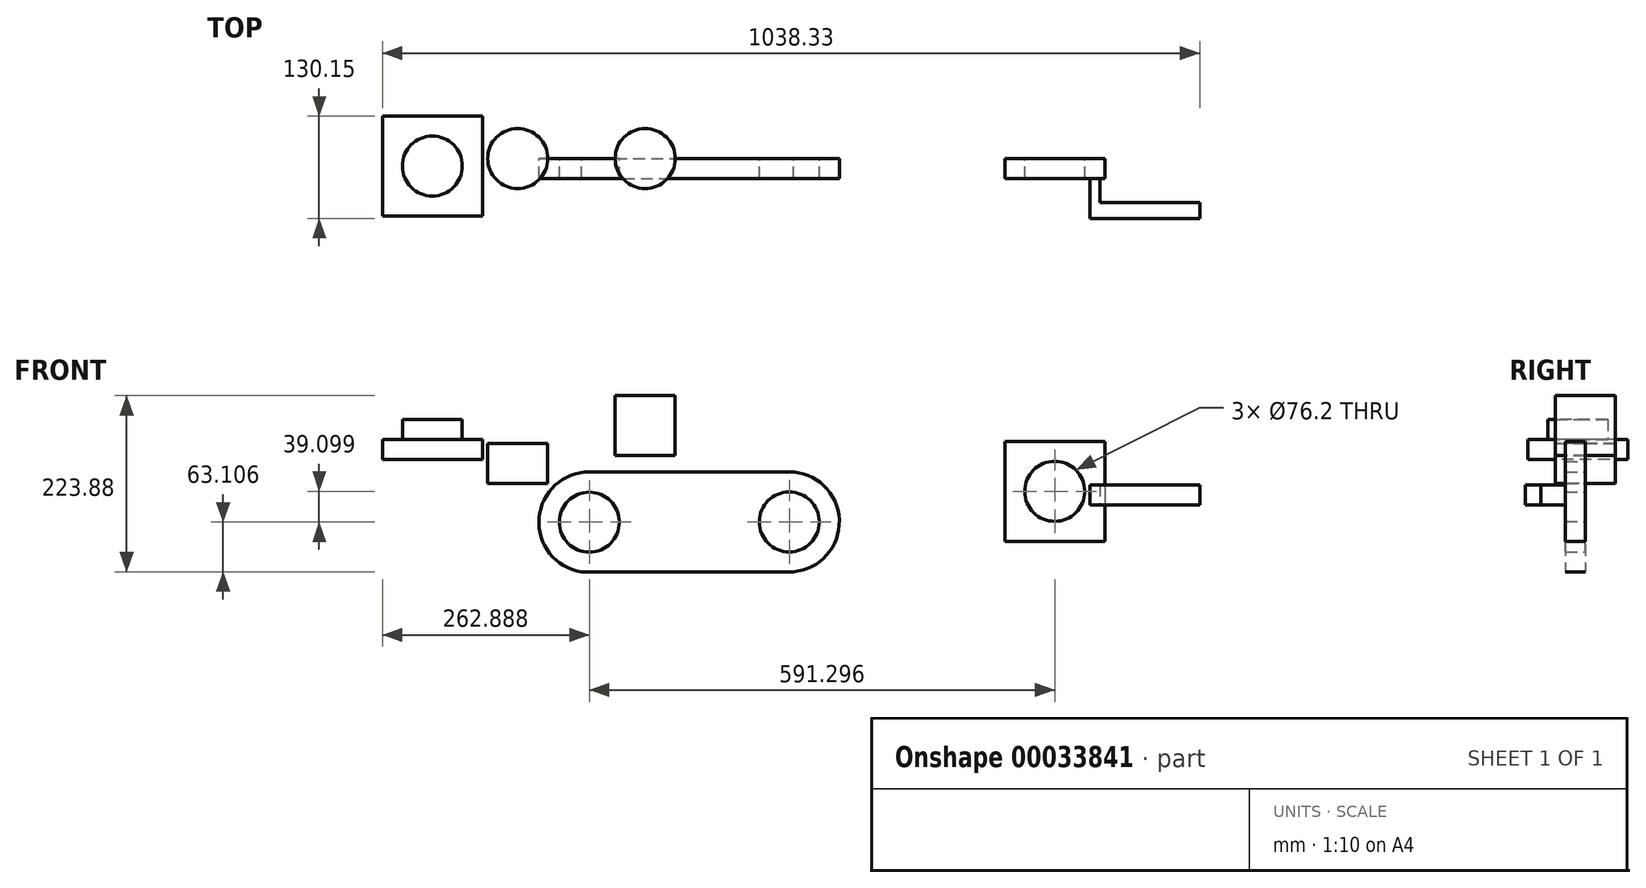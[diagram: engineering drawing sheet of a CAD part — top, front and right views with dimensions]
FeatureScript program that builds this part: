
annotation { "Feature Type Name" : "Feature", "Feature Type Description" : "" }
export const myFeature = defineFeature(function(context is Context, id is Id, definition is map)
    precondition{}
    {
        {
            var Q0;
            Q0=qCreatedBy(makeId("Top.planeOp"),FACE);
            var sketch = newSketch(context, id + "F0", { "sketchPlane" : qUnion([Q0])});
            skLineSegment(sketch, "E0.right", {"start": v(-80.77, 53.95) * mm, "end": v(-80.77, -73.05) * mm});
            skLineSegment(sketch, "E0.left", {"start": v(-207.77, 53.95) * mm, "end": v(-207.77, -73.05) * mm});
            skLineSegment(sketch, "E0.top", {"start": v(-207.77, -73.05) * mm, "end": v(-80.77, -73.05) * mm});
            skLineSegment(sketch, "E0.bottom", {"start": v(-207.77, 53.95) * mm, "end": v(-80.77, 53.95) * mm});
            skSolve(sketch);
        }
        {
            var Q0;
            Q0=makeQuery(id+"F0.imprint","IMPRINT",FACE,{"disambiguationData":[TD([[makeQuery(id+"F0.imprint","IMPRINT",EDGE,{"derivedFrom":sQuery(id+"F0.wireOp",EDGE,"E0.right")}),-1.0]])]});
            extrude(context, id + "F1", {"entities" : qUnion([Q0]), "depth" : 25.4 * mm});
        }
        {
            var Q0;
            Q0=makeQuery(id+"F1.opExtrude","CAP_FACE",FACE,{"disambiguationData":[OSD([sQuery(id+"F0.wireOp",EDGE,"E0.right"),sQuery(id+"F0.wireOp",EDGE,"E0.left"),sQuery(id+"F0.wireOp",EDGE,"E0.top"),sQuery(id+"F0.wireOp",EDGE,"E0.bottom")])],"isStart":false});
            var sketch = newSketch(context, id + "F2", { "sketchPlane" : qUnion([Q0])});
            skCircle(sketch, "E1", {"center": v(-144.27, -9.55) * mm, "radius": 38.1 * mm});
            skPoint(sketch, "E1.centerSnap0", {"position": v(-80.77, -9.55) * mm});
            skPoint(sketch, "E1.centerSnap1", {"position": v(-144.27, 53.95) * mm});
            skSolve(sketch);
        }
        {
            var Q0;
            Q0=makeQuery(id+"F2.imprint","IMPRINT",FACE,{"disambiguationData":[TD([[makeQuery(id+"F2.imprint","IMPRINT",EDGE,{"derivedFrom":sQuery(id+"F2.wireOp",EDGE,"E1")}),1.0]])]});
            extrude(context, id + "F3", {"entities" : qUnion([Q0]), "depth" : 25.4 * mm});
        }
        {
            var Q0;
            Q0=qCreatedBy(makeId("Front.planeOp"),FACE);
            var sketch = newSketch(context, id + "F4", { "sketchPlane" : qUnion([Q0])});
            skCircle(sketch, "E2", {"center": v(309.12, -79.39) * mm, "radius": 38.1 * mm});
            skLineSegment(sketch, "E3", {"start": v(55.12, -15.79) * mm, "end": v(309.12, -15.79) * mm});
            skCircle(sketch, "E4", {"center": v(55.12, -79.68) * mm, "radius": 38.1 * mm});
            skArc(sketch, "E5", {"start": v(314.23, -142.79) * mm, "mid": v(372.67, -76.83) * mm, "end": v(309.12, -15.79) * mm});
            skLineSegment(sketch, "E6", {"start": v(45.07, -142.79) * mm, "end": v(314.23, -142.79) * mm});
            skArc(sketch, "E7", {"start": v(55.12, -15.79) * mm, "mid": v(-8.58, -74.65) * mm, "end": v(45.07, -142.79) * mm});
            skLineSegment(sketch, "E8", {"start": v(55.67, -10.55) * mm, "end": v(55.12, -15.79) * mm});
            skSolve(sketch);
        }
        {
            var Q0;
            Q0=makeQuery(id+"F4.imprint","IMPRINT",FACE,{"disambiguationData":[TD([[makeQuery(id+"F4.imprint","IMPRINT",EDGE,{"derivedFrom":sQuery(id+"F4.wireOp",EDGE,"E2")}),-1.0]])]});
            extrude(context, id + "F5", {"entities" : qUnion([Q0]), "depth" : 25.4 * mm});
        }
        {
            var Q0;
            Q0=qCreatedBy(makeId("Front.planeOp"),FACE);
            var sketch = newSketch(context, id + "F6", { "sketchPlane" : qUnion([Q0])});
            skLineSegment(sketch, "E9", {"start": v(-35.84, 19.93) * mm, "end": v(-35.84, -38.25) * mm, "construction": true});
            skLineSegment(sketch, "E10.bottom", {"start": v(-35.84, 19.93) * mm, "end": v(2.26, 19.93) * mm});
            skLineSegment(sketch, "E10.top", {"start": v(-35.84, -30.87) * mm, "end": v(2.26, -30.87) * mm});
            skLineSegment(sketch, "E10.left", {"start": v(-35.84, 19.93) * mm, "end": v(-35.84, -30.87) * mm});
            skLineSegment(sketch, "E10.right", {"start": v(2.26, 19.93) * mm, "end": v(2.26, -30.87) * mm});
            skSolve(sketch);
        }
        {
            var Q0;
            Q0 = qSketchRegion(id + "F6", true);
            var Q1;
            Q1=sQuery(id+"F6.wireOp",EDGE,"E9");
            revolve(context, id + "F7", {"operationType" : NewBodyOperationType.ADD, "entities" : qUnion([Q0]), "axis" : qUnion([Q1]), "revolveType" : RevolveType.FULL});
        }
        {
            var Q0;
            Q0=qCreatedBy(makeId("Front.planeOp"),FACE);
            var sketch = newSketch(context, id + "F8", { "sketchPlane" : qUnion([Q0])});
            skLineSegment(sketch, "E11", {"start": v(126.09, 98.34) * mm, "end": v(126.09, 4.9) * mm});
            skLineSegment(sketch, "E12.bottom", {"start": v(126.09, 4.9) * mm, "end": v(164.19, 4.9) * mm});
            skLineSegment(sketch, "E12.left", {"start": v(126.09, 4.9) * mm, "end": v(126.09, 81.1) * mm, "construction": true});
            skLineSegment(sketch, "E12.right", {"start": v(164.19, 4.9) * mm, "end": v(164.19, 81.1) * mm});
            skLineSegment(sketch, "E13", {"start": v(126.09, 81.1) * mm, "end": v(126.09, 138.24) * mm});
            skLineSegment(sketch, "E14", {"start": v(126.09, 4.9) * mm, "end": v(126.09, 184.34) * mm, "construction": true});
            skLineSegment(sketch, "E15", {"start": v(126.09, 81.1) * mm, "end": v(164.19, 81.1) * mm});
            skSolve(sketch);
        }
        {
            var Q0;
            {var subQ2=sQuery(id+"F8.wireOp",EDGE,"E11");Q0=makeQuery(id+"F8.imprint","IMPRINT",FACE,{"disambiguationData":[TD([[makeQuery(id+"F8.imprint","IMPRINT",EDGE,{"derivedFrom":subQ2}),1.0]])]});}
            var Q1;
            Q1=sQuery(id+"F8.wireOp",EDGE,"E14");
            revolve(context, id + "F9", {"entities" : qUnion([Q0]), "axis" : qUnion([Q1]), "revolveType" : RevolveType.FULL});
        }
        {
            var Q0;
            Q0=qCreatedBy(makeId("Front.planeOp"),FACE);
            var sketch = newSketch(context, id + "F10", { "sketchPlane" : qUnion([Q0])});
            skLineSegment(sketch, "E16.bottom", {"start": v(23.04, 75.9) * mm, "end": v(23.3, 75.9) * mm});
            skLineSegment(sketch, "E16.top", {"start": v(23.04, 81.26) * mm, "end": v(23.3, 81.26) * mm});
            skLineSegment(sketch, "E17.bottom", {"start": v(582.91, 22.92) * mm, "end": v(709.91, 22.92) * mm});
            skLineSegment(sketch, "E17.top", {"start": v(582.91, -104.08) * mm, "end": v(709.91, -104.08) * mm});
            skLineSegment(sketch, "E17.left", {"start": v(582.91, 22.92) * mm, "end": v(582.91, -104.08) * mm});
            skCircle(sketch, "E18", {"center": v(646.41, -40.58) * mm, "radius": 38.1 * mm});
            skLineSegment(sketch, "E19", {"start": v(709.91, 22.92) * mm, "end": v(709.91, -104.08) * mm});
            skSolve(sketch);
        }
        {
            var Q0;
            Q0=makeQuery(id+"F10.imprint","IMPRINT",FACE,{"disambiguationData":[TD([[makeQuery(id+"F10.imprint","IMPRINT",EDGE,{"derivedFrom":sQuery(id+"F10.wireOp",EDGE,"E17.bottom")}),-1.0]])]});
            extrude(context, id + "F11", {"entities" : qUnion([Q0]), "depth" : 25.4 * mm});
        }
        {
            var Q0;
            Q0=makeQuery(id+"F11.opExtrude","CAP_FACE",FACE,{"disambiguationData":[OSD([sQuery(id+"F10.wireOp",EDGE,"E17.bottom"),sQuery(id+"F10.wireOp",EDGE,"E17.top"),sQuery(id+"F10.wireOp",EDGE,"E17.left"),sQuery(id+"F10.wireOp",EDGE,"E18"),sQuery(id+"F10.wireOp",EDGE,"E19")])],"isStart":false});
            var sketch = newSketch(context, id + "F12", { "sketchPlane" : qUnion([Q0])});
            skPoint(sketch, "E20.firstSnap0", {"position": v(709.91, -40.58) * mm});
            skLineSegment(sketch, "E20.left", {"start": v(704.72, -40.58) * mm, "end": v(704.72, -39.11) * mm});
            skLineSegment(sketch, "E20.right", {"start": v(692.02, -40.58) * mm, "end": v(692.02, -39.11) * mm});
            skLineSegment(sketch, "E21", {"start": v(709.91, -40.58) * mm, "end": v(684.51, -40.58) * mm});
            skLineSegment(sketch, "E22.bottom", {"start": v(690.86, -32.33) * mm, "end": v(703.56, -32.33) * mm});
            skLineSegment(sketch, "E22.top", {"start": v(690.86, -57.73) * mm, "end": v(703.56, -57.73) * mm});
            skLineSegment(sketch, "E22.left", {"start": v(690.86, -32.33) * mm, "end": v(690.86, -57.73) * mm});
            skLineSegment(sketch, "E22.right", {"start": v(703.56, -32.33) * mm, "end": v(703.56, -57.73) * mm});
            skSolve(sketch);
        }
        {
            var Q0;
            {var subQ3=sQuery(id+"F12.wireOp",EDGE,"E22.top");Q0=makeQuery(id+"F12.imprint","IMPRINT",FACE,{"disambiguationData":[TD([[makeQuery(id+"F12.imprint","IMPRINT",EDGE,{"derivedFrom":subQ3}),1.0]])]});}
            var Q1;
            {var subQ3=sQuery(id+"F12.wireOp",EDGE,"E22.bottom");Q1=makeQuery(id+"F12.imprint","IMPRINT",FACE,{"disambiguationData":[TD([[makeQuery(id+"F12.imprint","IMPRINT",EDGE,{"derivedFrom":subQ3}),-1.0]])]});}
            extrude(context, id + "F13", {"entities" : qUnion([Q0, Q1]), "operationType" : NewBodyOperationType.ADD, "depth" : 50.8 * mm});
        }
        {
            var Q0;
            Q0=makeQuery(id+"F13.opExtrude","SWEPT_FACE",FACE,{"disambiguationData":[OSD([sQuery(id+"F12.wireOp",EDGE,"E22.right")])]});
            var sketch = newSketch(context, id + "F14", { "sketchPlane" : qUnion([Q0])});
            skLineSegment(sketch, "E23.bottom", {"start": v(-76.2, -32.33) * mm, "end": v(-56.25, -32.33) * mm});
            skLineSegment(sketch, "E23.top", {"start": v(-76.2, -57.73) * mm, "end": v(-56.25, -57.73) * mm});
            skLineSegment(sketch, "E23.left", {"start": v(-76.2, -32.33) * mm, "end": v(-76.2, -57.73) * mm});
            skLineSegment(sketch, "E23.right", {"start": v(-56.25, -32.33) * mm, "end": v(-56.25, -57.73) * mm});
            skSolve(sketch);
        }
        {
            var Q0;
            Q0=makeQuery(id+"F14.imprint","IMPRINT",FACE,{"disambiguationData":[TD([[makeQuery(id+"F14.imprint","IMPRINT",EDGE,{"derivedFrom":sQuery(id+"F14.wireOp",EDGE,"E23.bottom")}),-1.0]])]});
            extrude(context, id + "F15", {"entities" : qUnion([Q0]), "operationType" : NewBodyOperationType.ADD, "depth" : 127 * mm});
        }
    });
